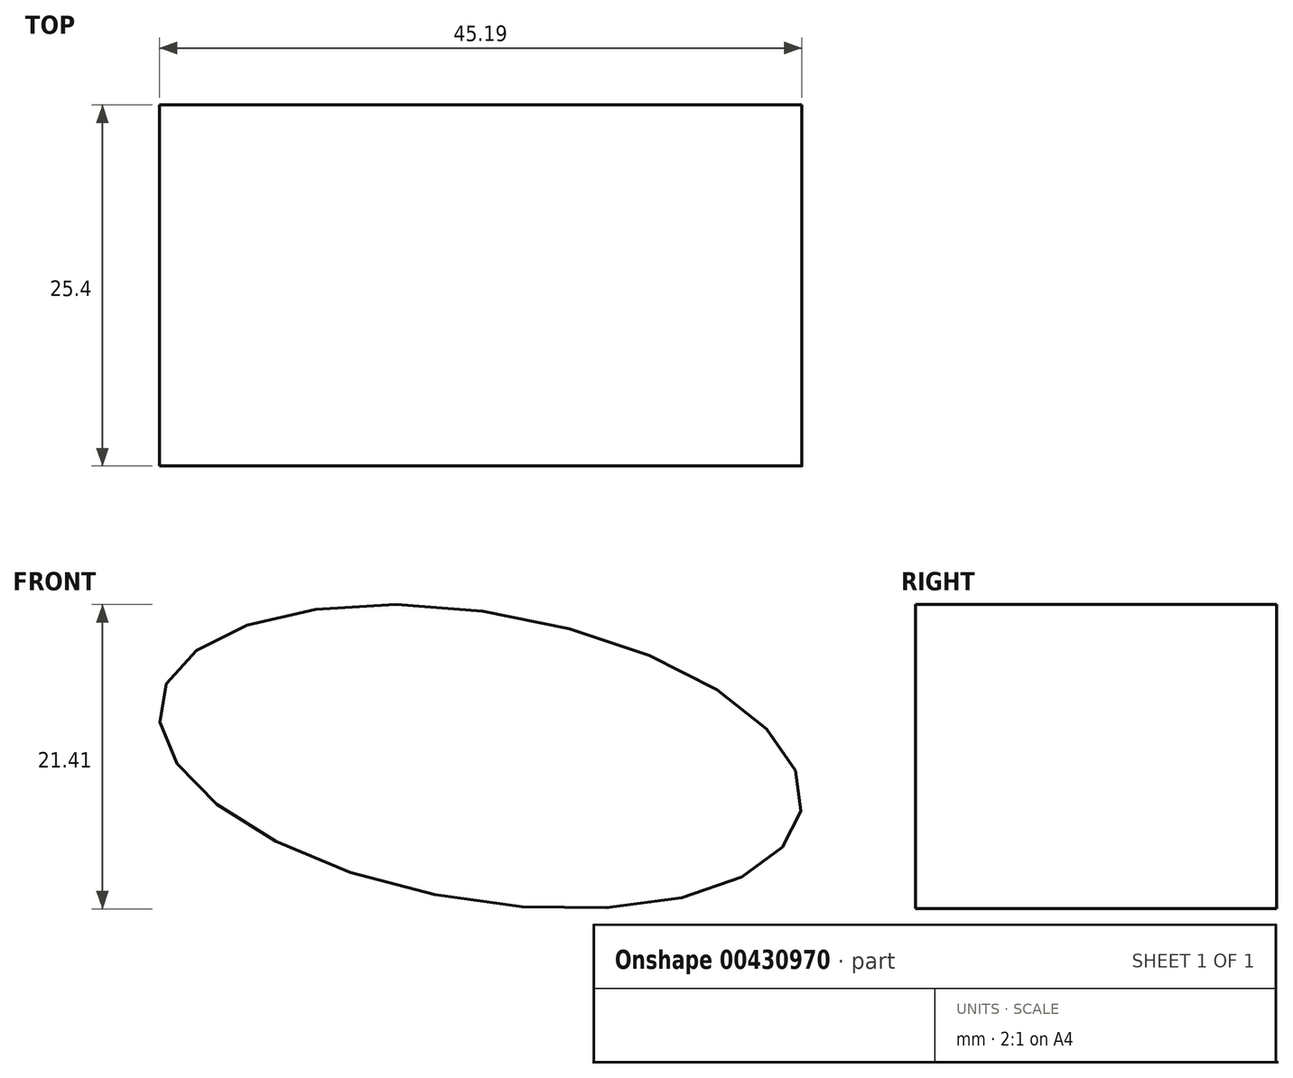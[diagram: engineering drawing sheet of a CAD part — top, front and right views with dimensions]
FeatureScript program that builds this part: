
annotation { "Feature Type Name" : "Feature", "Feature Type Description" : "" }
export const myFeature = defineFeature(function(context is Context, id is Id, definition is map)
    precondition{}
    {
        {
            var Q0;
            Q0=qCreatedBy(makeId("Front.planeOp"),FACE);
            var sketch = newSketch(context, id + "F0", { "sketchPlane" : qUnion([Q0])});
            skEllipse(sketch, "E0", {"center": v(-26.7, 45.94) * mm, "majorRadius": 22.85 * mm, "minorRadius": 10.14 * mm, "majorAxis": v(0.99, -0.17)});
            skSolve(sketch);
        }
        {
            var Q0;
            Q0=sQuery(id+"F0.wireOp",EDGE,"E0");
            extrude(context, id + "F1", {"bodyType" : ToolBodyType.SURFACE, "surfaceEntities" : qUnion([Q0]), "depth" : 25.4 * mm});
        }
    });
